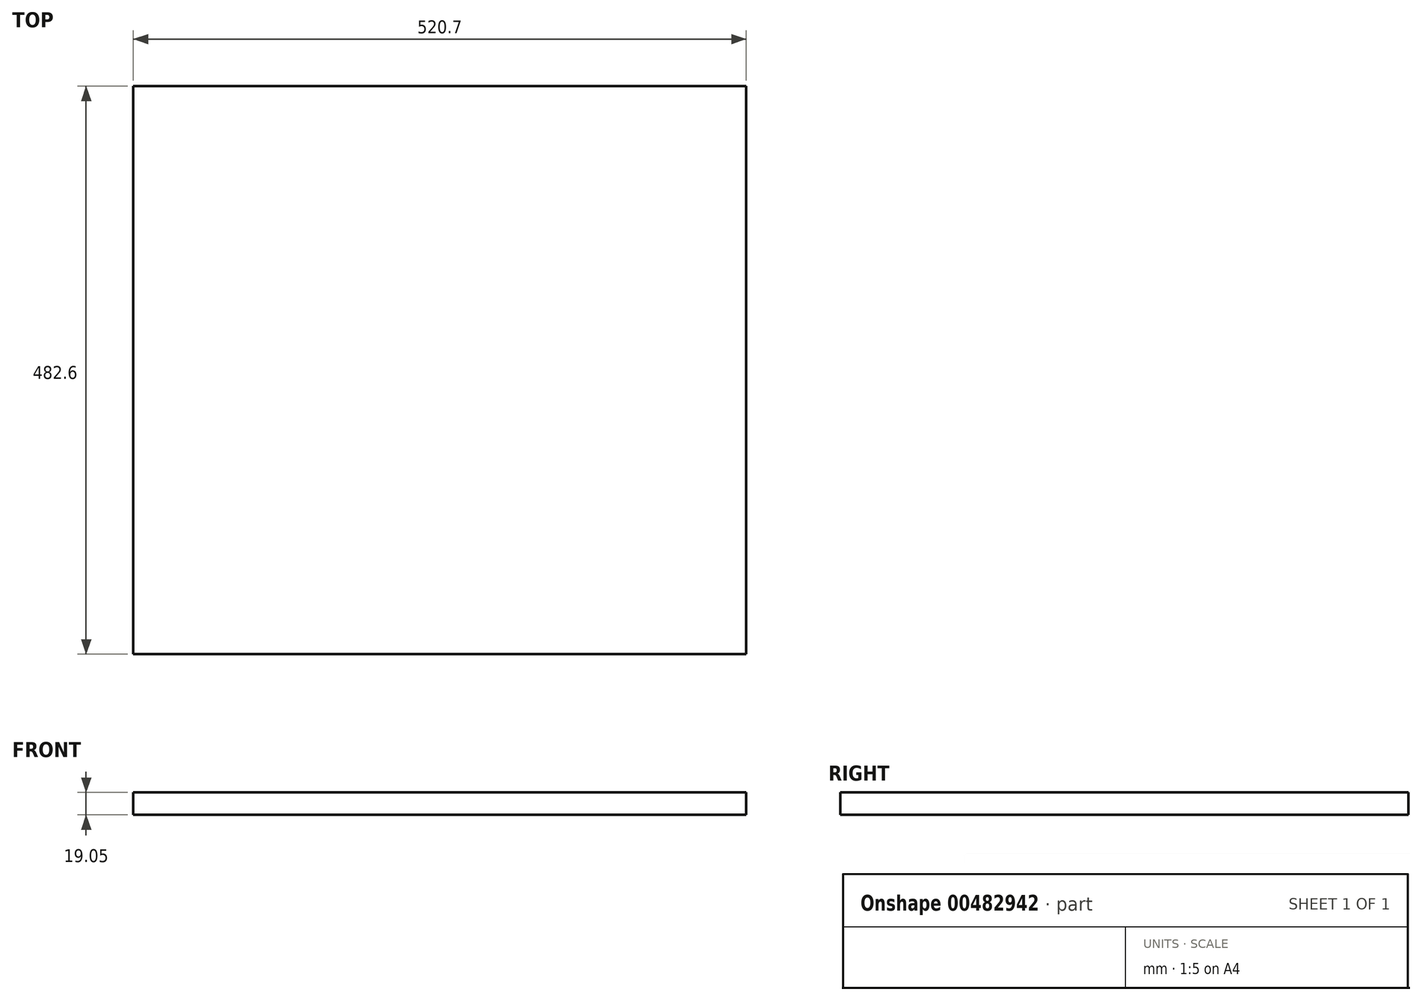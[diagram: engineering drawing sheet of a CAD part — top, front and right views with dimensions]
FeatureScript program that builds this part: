
annotation { "Feature Type Name" : "Feature", "Feature Type Description" : "" }
export const myFeature = defineFeature(function(context is Context, id is Id, definition is map)
    precondition{}
    {
        {
            var Q0;
            Q0=qCreatedBy(makeId("Top.planeOp"),FACE);
            var sketch = newSketch(context, id + "F0", { "sketchPlane" : qUnion([Q0])});
            skLineSegment(sketch, "E0.bottom", {"start": v(260.35, -241.3) * mm, "end": v(-260.35, -241.3) * mm});
            skLineSegment(sketch, "E0.top", {"start": v(260.35, 241.3) * mm, "end": v(-260.35, 241.3) * mm});
            skLineSegment(sketch, "E0.left", {"start": v(260.35, -241.3) * mm, "end": v(260.35, 241.3) * mm});
            skLineSegment(sketch, "E0.right", {"start": v(-260.35, -241.3) * mm, "end": v(-260.35, 241.3) * mm});
            skPoint(sketch, "E0.middle", {"position": v(0, 0) * mm});
            skSolve(sketch);
        }
        {
            var Q0;
            Q0=makeQuery(id+"F0.imprint","IMPRINT",FACE,{"disambiguationData":[TD([[makeQuery(id+"F0.imprint","IMPRINT",EDGE,{"derivedFrom":sQuery(id+"F0.wireOp",EDGE,"E0.bottom")}),-1.0]])]});
            extrude(context, id + "F1", {"entities" : qUnion([Q0]), "depth" : 19.05 * mm});
        }
    });
